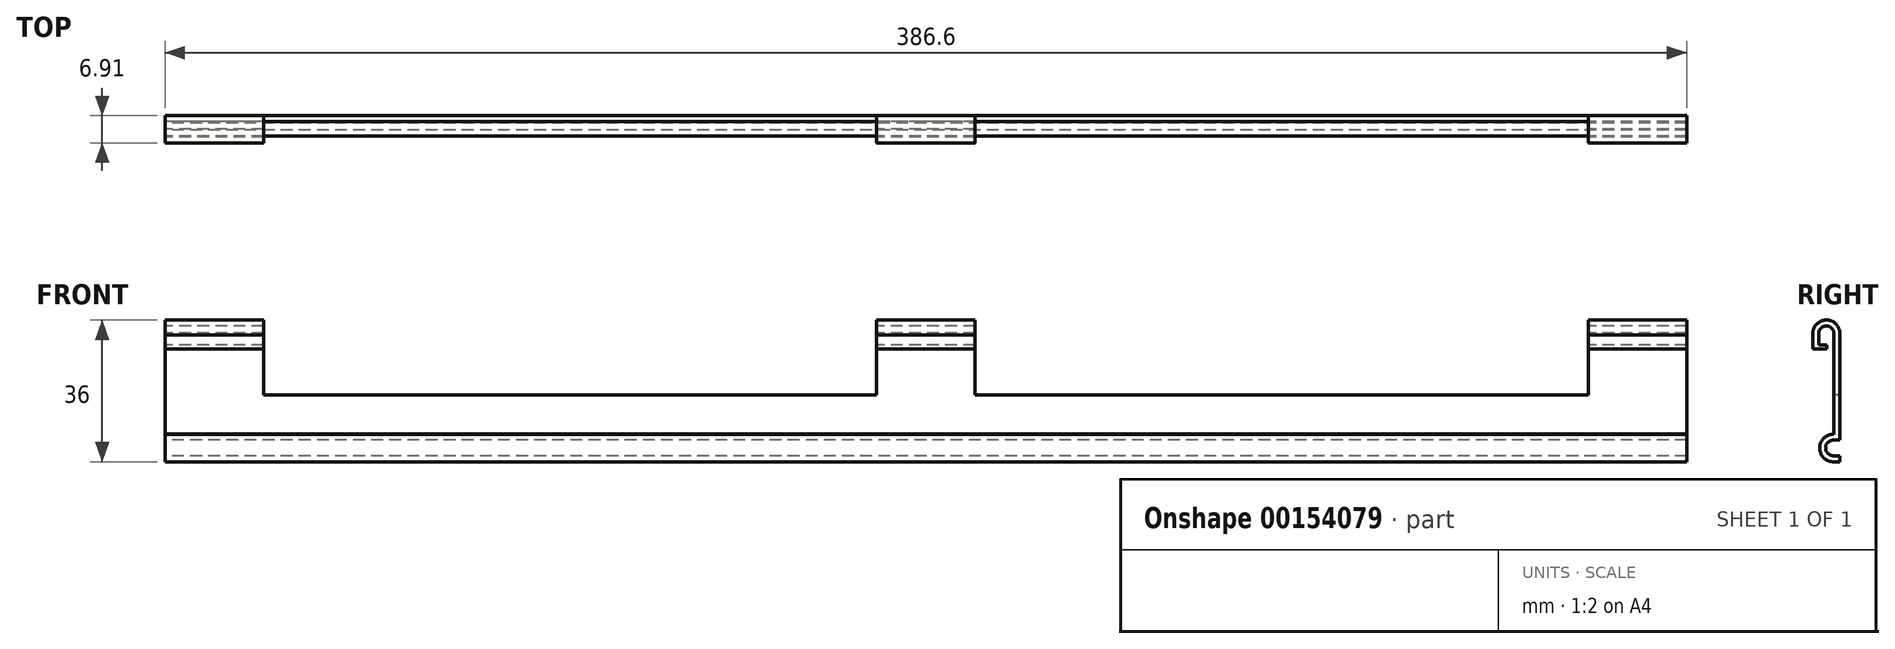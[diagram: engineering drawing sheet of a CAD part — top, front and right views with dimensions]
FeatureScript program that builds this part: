
annotation { "Feature Type Name" : "Feature", "Feature Type Description" : "" }
export const myFeature = defineFeature(function(context is Context, id is Id, definition is map)
    precondition{}
    {
        {
            var Q0;
            Q0=qCreatedBy(makeId("Right.planeOp"),FACE);
            var sketch = newSketch(context, id + "F0", { "sketchPlane" : qUnion([Q0])});
            skLineSegment(sketch, "E0", {"start": v(0, -15.5) * mm, "end": v(-1.64, -15.5) * mm});
            skArc(sketch, "E1", {"start": v(-1.64, -15.5) * mm, "mid": v(-3.64, -13.6) * mm, "end": v(-1.83, -11.52) * mm});
            skLineSegment(sketch, "E2", {"start": v(-1.83, -11.52) * mm, "end": v(0, -11.52) * mm});
            skLineSegment(sketch, "E3", {"start": v(0, -11.52) * mm, "end": v(0, 15.54) * mm});
            skArc(sketch, "E4", {"start": v(0, 15.54) * mm, "mid": v(-3.6, 18.99) * mm, "end": v(-6.9, 15.25) * mm});
            skLineSegment(sketch, "E5", {"start": v(-6.9, 15.25) * mm, "end": v(-6.9, 11.65) * mm});
            skArc(sketch, "E6.0", {"start": v(-1.64, -17) * mm, "mid": v(-5.14, -13.44) * mm, "end": v(-1.5, -10.01) * mm});
            skLineSegment(sketch, "E6.1", {"start": v(0, -17) * mm, "end": v(-1.64, -17) * mm});
            skLineSegment(sketch, "E7", {"start": v(-6.9, 11.65) * mm, "end": v(-3.37, 11.65) * mm});
            skLineSegment(sketch, "E8", {"start": v(-3.37, 11.65) * mm, "end": v(-3.37, 12.62) * mm});
            skLineSegment(sketch, "E9", {"start": v(-3.37, 12.62) * mm, "end": v(-5.41, 12.62) * mm});
            skLineSegment(sketch, "E10", {"start": v(-5.41, 12.62) * mm, "end": v(-5.41, 15.54) * mm});
            skArc(sketch, "E11", {"start": v(-5.41, 15.54) * mm, "mid": v(-3.51, 17.5) * mm, "end": v(-1.5, 15.66) * mm});
            skLineSegment(sketch, "E12", {"start": v(-1.5, 15.66) * mm, "end": v(-1.5, -10.01) * mm});
            skLineSegment(sketch, "E13", {"start": v(0, -17) * mm, "end": v(0, -15.5) * mm});
            skSolve(sketch);
        }
        {
            var Q0;
            Q0 = qSketchRegion(id + "F0", true);
            extrude(context, id + "F1", {"entities" : qUnion([Q0]), "endBound" : BoundingType.SYMMETRIC, "depth" : 386.6 * mm});
        }
        {
            var Q0;
            Q0=qCreatedBy(makeId("Front.planeOp"),FACE);
            var sketch = newSketch(context, id + "F2", { "sketchPlane" : qUnion([Q0])});
            skLineSegment(sketch, "E14.bottom", {"start": v(-168.3, 27.63) * mm, "end": v(-12.5, 27.63) * mm});
            skLineSegment(sketch, "E14.top", {"start": v(-168.3, 0) * mm, "end": v(-12.5, 0) * mm});
            skLineSegment(sketch, "E14.left", {"start": v(-168.3, 27.63) * mm, "end": v(-168.3, 0) * mm});
            skLineSegment(sketch, "E14.right", {"start": v(-12.5, 27.63) * mm, "end": v(-12.5, 0) * mm});
            skLineSegment(sketch, "E15.bottom", {"start": v(12.5, 29.05) * mm, "end": v(168.3, 29.05) * mm});
            skLineSegment(sketch, "E15.top", {"start": v(12.5, 0) * mm, "end": v(168.3, 0) * mm});
            skLineSegment(sketch, "E15.left", {"start": v(12.5, 29.05) * mm, "end": v(12.5, 0) * mm});
            skLineSegment(sketch, "E15.right", {"start": v(168.3, 29.05) * mm, "end": v(168.3, 0) * mm});
            skSolve(sketch);
        }
        {
            var Q0;
            Q0 = qSketchRegion(id + "F2", true);
            extrude(context, id + "F3", {"entities" : qUnion([Q0]), "operationType" : NewBodyOperationType.REMOVE, "endBound" : BoundingType.THROUGH_ALL, "oppositeDirection" : true, "depth" : 25 * mm, "hasSecondDirection" : true, "secondDirectionBound" : SecondDirectionBoundingType.THROUGH_ALL, "secondDirectionOppositeDirection" : false, "secondDirectionDepth" : 25 * mm});
        }
    });
